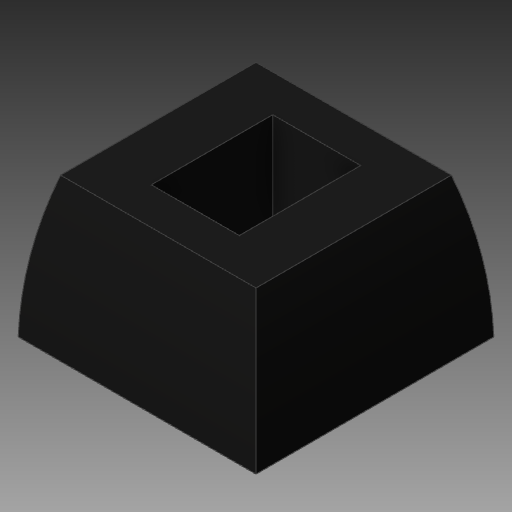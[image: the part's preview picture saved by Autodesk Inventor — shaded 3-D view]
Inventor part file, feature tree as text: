
AUTODESK INVENTOR PART (.ipt)
format: ipt  version: 2018 (Build 220112000, 112)  size: 135,168 bytes
history: native  units: mm
features: other x7, loft x1, extrude x1
ambient origin geometry x8: Origin, YZ Plane, XZ Plane, XY Plane, X Axis, Y Axis, Z Axis, Center Point
bodies: Solid1 (feature_tree)
feature tree (9):
  other  "Base Loop"
  other  "Mid Plane"
  other  "Mid Loop"
  other  "Top Plane"
  loft  "Keyswitch Body"
  extrude  "Pole Cut in"  Depth=14.6mm
  other  "Base Plane"
  other  "Top Loop"
  other  "Cut in profile"
